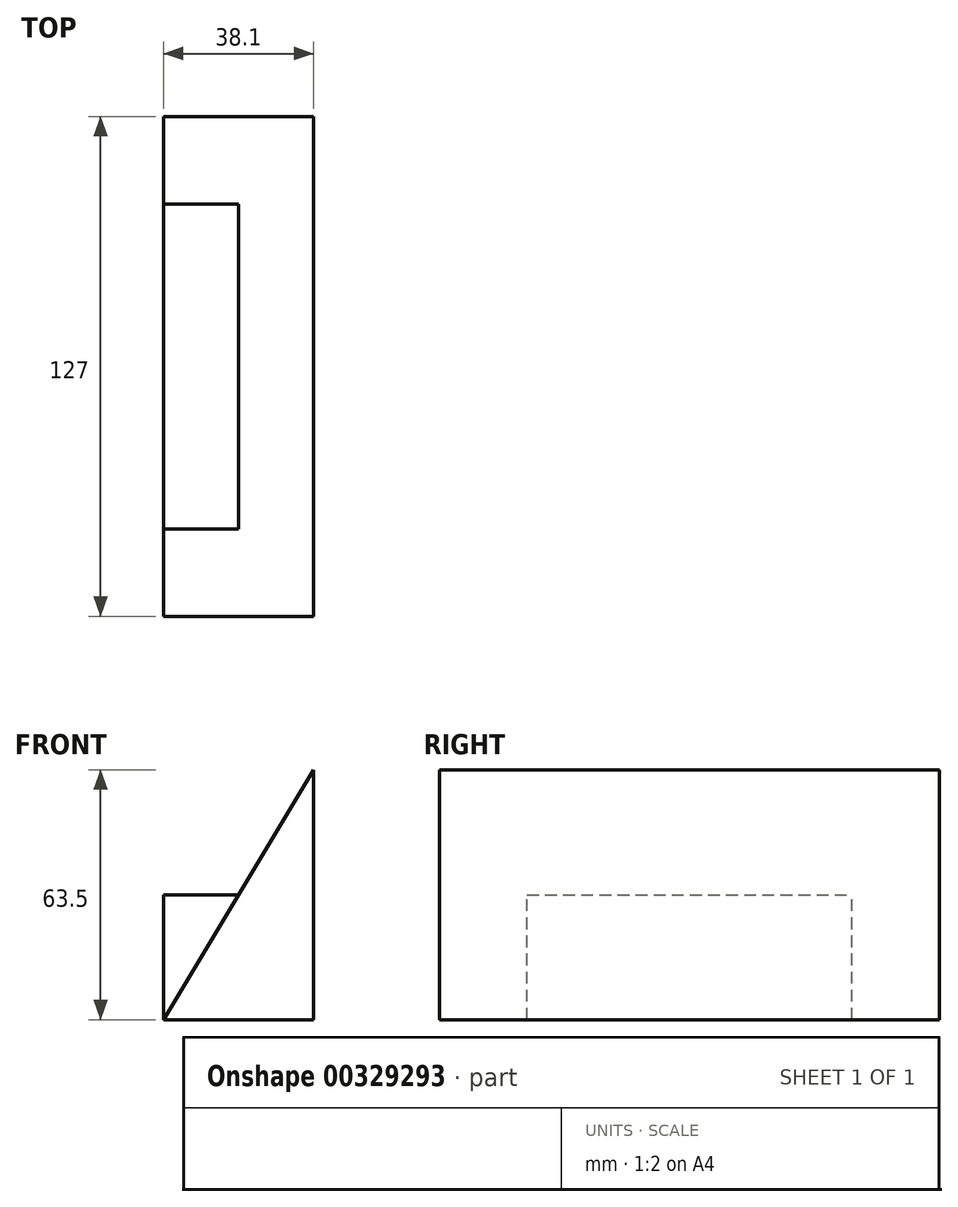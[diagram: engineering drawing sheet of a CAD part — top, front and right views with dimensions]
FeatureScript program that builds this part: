
annotation { "Feature Type Name" : "Feature", "Feature Type Description" : "" }
export const myFeature = defineFeature(function(context is Context, id is Id, definition is map)
    precondition{}
    {
        {
            var Q0;
            Q0=qCreatedBy(makeId("Front.planeOp"),FACE);
            var sketch = newSketch(context, id + "F0", { "sketchPlane" : qUnion([Q0])});
            skLineSegment(sketch, "E0", {"start": v(51.5, -35.12) * mm, "end": v(51.5, 28.38) * mm});
            skLineSegment(sketch, "E1", {"start": v(51.5, -35.12) * mm, "end": v(13.4, -35.12) * mm});
            skLineSegment(sketch, "E2", {"start": v(13.4, -35.12) * mm, "end": v(51.5, 28.38) * mm});
            skPoint(sketch, "E3", {"position": v(51.5, -3.37) * mm});
            skLineSegment(sketch, "E4", {"start": v(32.46, -3.37) * mm, "end": v(13.4, -3.37) * mm});
            skLineSegment(sketch, "E5", {"start": v(13.4, -3.37) * mm, "end": v(13.4, -35.12) * mm});
            skSolve(sketch);
        }
        {
            var Q0;
            {var subQ0=sQuery(id+"F0.wireOp",EDGE,"E0");Q0=makeQuery(id+"F0.imprint","IMPRINT",FACE,{"disambiguationData":[TD([[makeQuery(id+"F0.imprint","IMPRINT",EDGE,{"derivedFrom":subQ0}),1.0]])]});}
            extrude(context, id + "F1", {"entities" : qUnion([Q0]), "depth" : 63.5 * mm});
        }
        {
            var Q0;
            Q0=makeQuery(id+"F1.opExtrude","CAP_FACE",FACE,{"disambiguationData":[OSD([sQuery(id+"F0.wireOp",EDGE,"E0"),sQuery(id+"F0.wireOp",EDGE,"E1"),sQuery(id+"F0.wireOp",EDGE,"E2")])],"isStart":true});
            extrude(context, id + "F2", {"entities" : qUnion([Q0]), "operationType" : NewBodyOperationType.ADD, "depth" : 63.5 * mm});
        }
        {
            var Q0;
            Q0 = qSketchRegion(id + "F0", true);
            extrude(context, id + "F3", {"entities" : qUnion([Q0]), "operationType" : NewBodyOperationType.ADD, "depth" : 41.27 * mm});
        }
        {
            var Q0;
            Q0=makeQuery(id+"F3.opExtrude","CAP_FACE",FACE,{"disambiguationData":[OSD([sQuery(id+"F0.wireOp",EDGE,"E0"),sQuery(id+"F0.wireOp",EDGE,"E1"),sQuery(id+"F0.wireOp",EDGE,"E2"),sQuery(id+"F0.wireOp",EDGE,"E4"),sQuery(id+"F0.wireOp",EDGE,"E5")])],"isStart":true});
            extrude(context, id + "F4", {"entities" : qUnion([Q0]), "operationType" : NewBodyOperationType.ADD, "depth" : 41.27 * mm});
        }
    });
